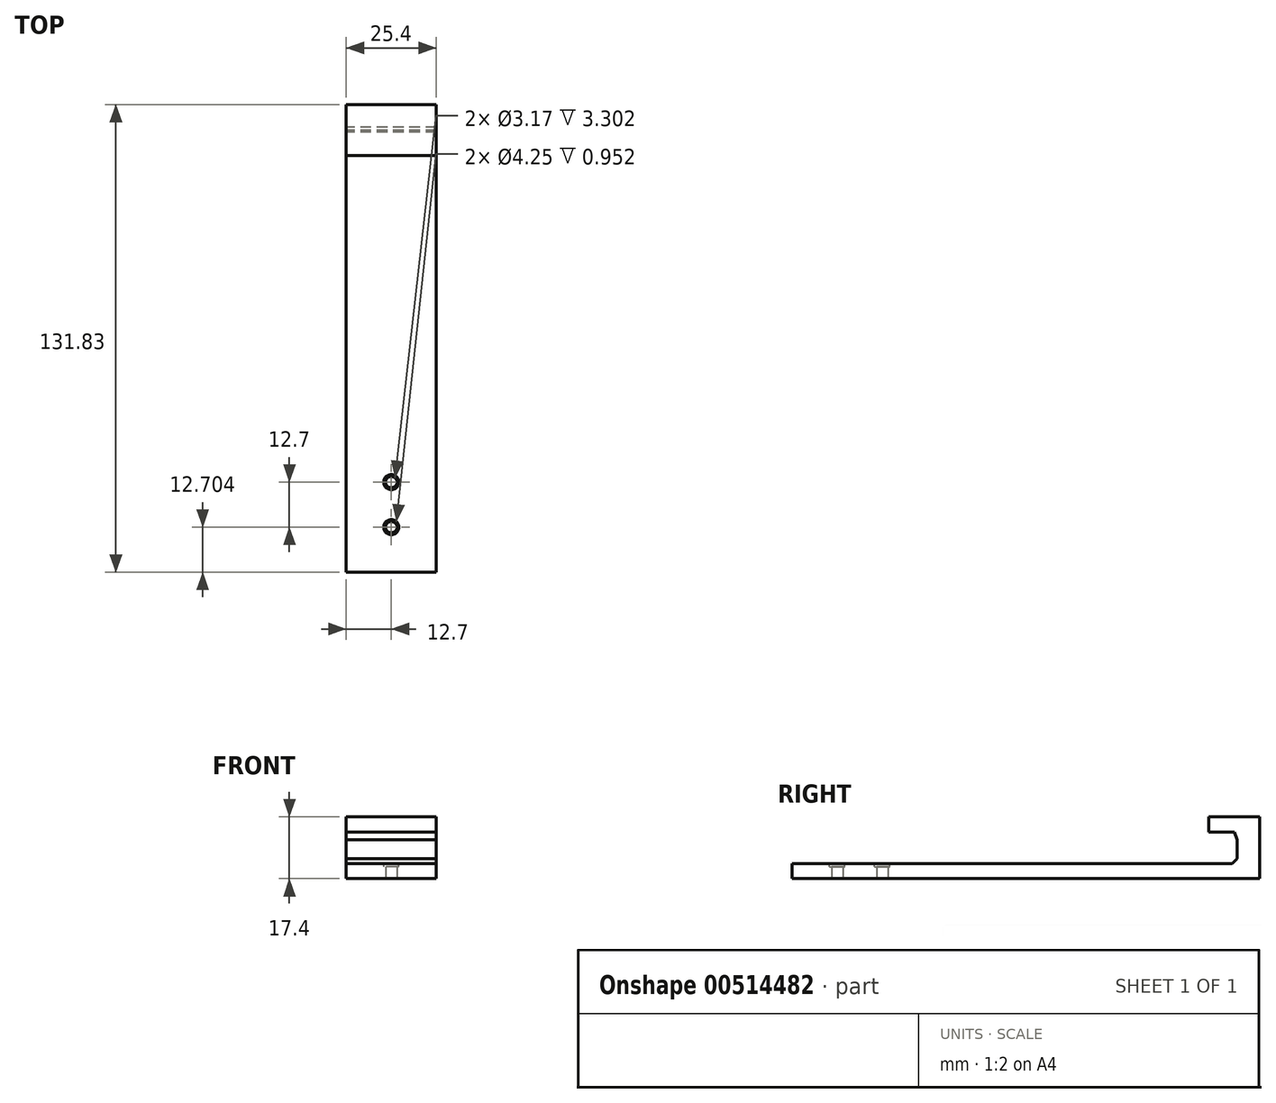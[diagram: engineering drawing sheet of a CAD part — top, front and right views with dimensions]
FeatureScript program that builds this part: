
annotation { "Feature Type Name" : "Feature", "Feature Type Description" : "" }
export const myFeature = defineFeature(function(context is Context, id is Id, definition is map)
    precondition{}
    {
        {
            var Q0;
            Q0=qCreatedBy(makeId("Right.planeOp"),FACE);
            var sketch = newSketch(context, id + "F0", { "sketchPlane" : qUnion([Q0])});
            skLineSegment(sketch, "E0.bottom", {"start": v(0, 0) * mm, "end": v(19.05, 0) * mm});
            skLineSegment(sketch, "E0.top", {"start": v(0, 4.25) * mm, "end": v(11.28, 4.25) * mm});
            skLineSegment(sketch, "E0.left", {"start": v(0, 0) * mm, "end": v(0, 4.25) * mm});
            skLineSegment(sketch, "E0.right", {"start": v(19.05, 0) * mm, "end": v(19.05, 4.25) * mm});
            skLineSegment(sketch, "E1.bottom", {"start": v(19.05, 0) * mm, "end": v(12.7, 0) * mm});
            skLineSegment(sketch, "E1.top", {"start": v(19.05, 17.4) * mm, "end": v(12.7, 17.4) * mm});
            skLineSegment(sketch, "E1.left", {"start": v(19.05, 0) * mm, "end": v(19.05, 17.4) * mm});
            skLineSegment(sketch, "E1.right", {"start": v(12.7, 5.65) * mm, "end": v(12.7, 11.02) * mm});
            skLineSegment(sketch, "E2.bottom", {"start": v(19.05, 17.4) * mm, "end": v(4.7, 17.4) * mm});
            skLineSegment(sketch, "E2.top", {"start": v(11.87, 13.14) * mm, "end": v(4.7, 13.14) * mm});
            skLineSegment(sketch, "E2.right", {"start": v(4.7, 17.4) * mm, "end": v(4.7, 13.14) * mm});
            skLineSegment(sketch, "E3", {"start": v(11.87, 13.14) * mm, "end": v(12.7, 11.02) * mm});
            skLineSegment(sketch, "E4", {"start": v(11.28, 4.25) * mm, "end": v(12.7, 5.65) * mm});
            skPoint(sketch, "E5.orphan", {"position": v(19.05, 13.14) * mm});
            skSolve(sketch);
        }
        {
            var Q0;
            Q0=makeQuery(id+"F0.imprint","IMPRINT",FACE,{"disambiguationData":[TD([[makeQuery(id+"F0.imprint","IMPRINT",EDGE,{"derivedFrom":sQuery(id+"F0.wireOp",EDGE,"E0.bottom")}),1.0]])]});
            extrude(context, id + "F1", {"entities" : qUnion([Q0]), "depth" : 25.4 * mm});
        }
        {
            var Q0;
            Q0=makeQuery(id+"F1.opExtrude","SWEPT_FACE",FACE,{"disambiguationData":[OSD([sQuery(id+"F0.wireOp",EDGE,"E0.left")])]});
            extrude(context, id + "F2", {"entities" : qUnion([Q0]), "operationType" : NewBodyOperationType.ADD, "depth" : 112.78 * mm});
        }
        {
            var Q0;
            {var subQ0=sQuery(id+"F0.wireOp",EDGE,"E0.bottom");Q0=makeQuery(id+"F2.boolean.opBoolean","MERGE",FACE,{"derivedFrom":[makeQuery(id+"F1.opExtrude","SWEPT_FACE",FACE,{"disambiguationData":[OSD([subQ0,sQuery(id+"F0.wireOp",EDGE,"E1.bottom")])]}),makeQuery(id+"F2.opExtrude","SWEPT_FACE",FACE,{"disambiguationData":[OSD([subQ0,sQuery(id+"F0.wireOp",EDGE,"E0.left")])]})]});}
            var sketch = newSketch(context, id + "F3", { "sketchPlane" : qUnion([Q0])});
            skCircle(sketch, "E6", {"center": v(12.7, 100.08) * mm, "radius": 1.59 * mm});
            skCircle(sketch, "E7", {"center": v(12.7, 87.38) * mm, "radius": 1.59 * mm});
            skPoint(sketch, "E8.left.start.orphan", {"position": v(9.52, 100.08) * mm});
            skPoint(sketch, "E9.orphan", {"position": v(9.53, 87.38) * mm});
            skPoint(sketch, "E8.right.end.orphan", {"position": v(15.88, 87.38) * mm});
            skPoint(sketch, "E10.orphan", {"position": v(15.88, 100.08) * mm});
            skSolve(sketch);
        }
        {
            var Q0;
            Q0=makeQuery(id+"F3.imprint","IMPRINT",FACE,{"disambiguationData":[TD([[makeQuery(id+"F3.imprint","IMPRINT",EDGE,{"derivedFrom":sQuery(id+"F3.wireOp",EDGE,"E6")}),1.0]])]});
            var Q1;
            Q1=makeQuery(id+"F3.imprint","IMPRINT",FACE,{"disambiguationData":[TD([[makeQuery(id+"F3.imprint","IMPRINT",EDGE,{"derivedFrom":sQuery(id+"F3.wireOp",EDGE,"E7")}),1.0]])]});
            extrude(context, id + "F4", {"entities" : qUnion([Q0, Q1]), "operationType" : NewBodyOperationType.REMOVE, "oppositeDirection" : true, "depth" : 25.4 * mm});
        }
        {
            var Q0;
            {var subQ0=sQuery(id+"F0.wireOp",EDGE,"E0.top");Q0=makeQuery(id+"F2.boolean.opBoolean","MERGE",FACE,{"derivedFrom":[makeQuery(id+"F1.opExtrude","SWEPT_FACE",FACE,{"disambiguationData":[OSD([subQ0])]}),makeQuery(id+"F2.opExtrude","SWEPT_FACE",FACE,{"disambiguationData":[OSD([subQ0,sQuery(id+"F0.wireOp",EDGE,"E0.left")])]})]});}
            var sketch = newSketch(context, id + "F5", { "sketchPlane" : qUnion([Q0])});
            skCircle(sketch, "E11", {"center": v(12.7, -87.38) * mm, "radius": 2.13 * mm});
            skCircle(sketch, "E12", {"center": v(12.7, -100.08) * mm, "radius": 2.13 * mm});
            skSolve(sketch);
        }
        {
            var Q0;
            Q0=makeQuery(id+"F5.imprint","IMPRINT",FACE,{"disambiguationData":[TD([[makeQuery(id+"F5.imprint","IMPRINT",EDGE,{"derivedFrom":sQuery(id+"F5.wireOp",EDGE,"E11")}),1.0]])]});
            var Q1;
            Q1=makeQuery(id+"F5.imprint","IMPRINT",FACE,{"disambiguationData":[TD([[makeQuery(id+"F5.imprint","IMPRINT",EDGE,{"derivedFrom":sQuery(id+"F5.wireOp",EDGE,"E12")}),1.0]])]});
            extrude(context, id + "F6", {"entities" : qUnion([Q0, Q1]), "operationType" : NewBodyOperationType.REMOVE, "oppositeDirection" : true, "depth" : 0.95 * mm});
        }
    });
